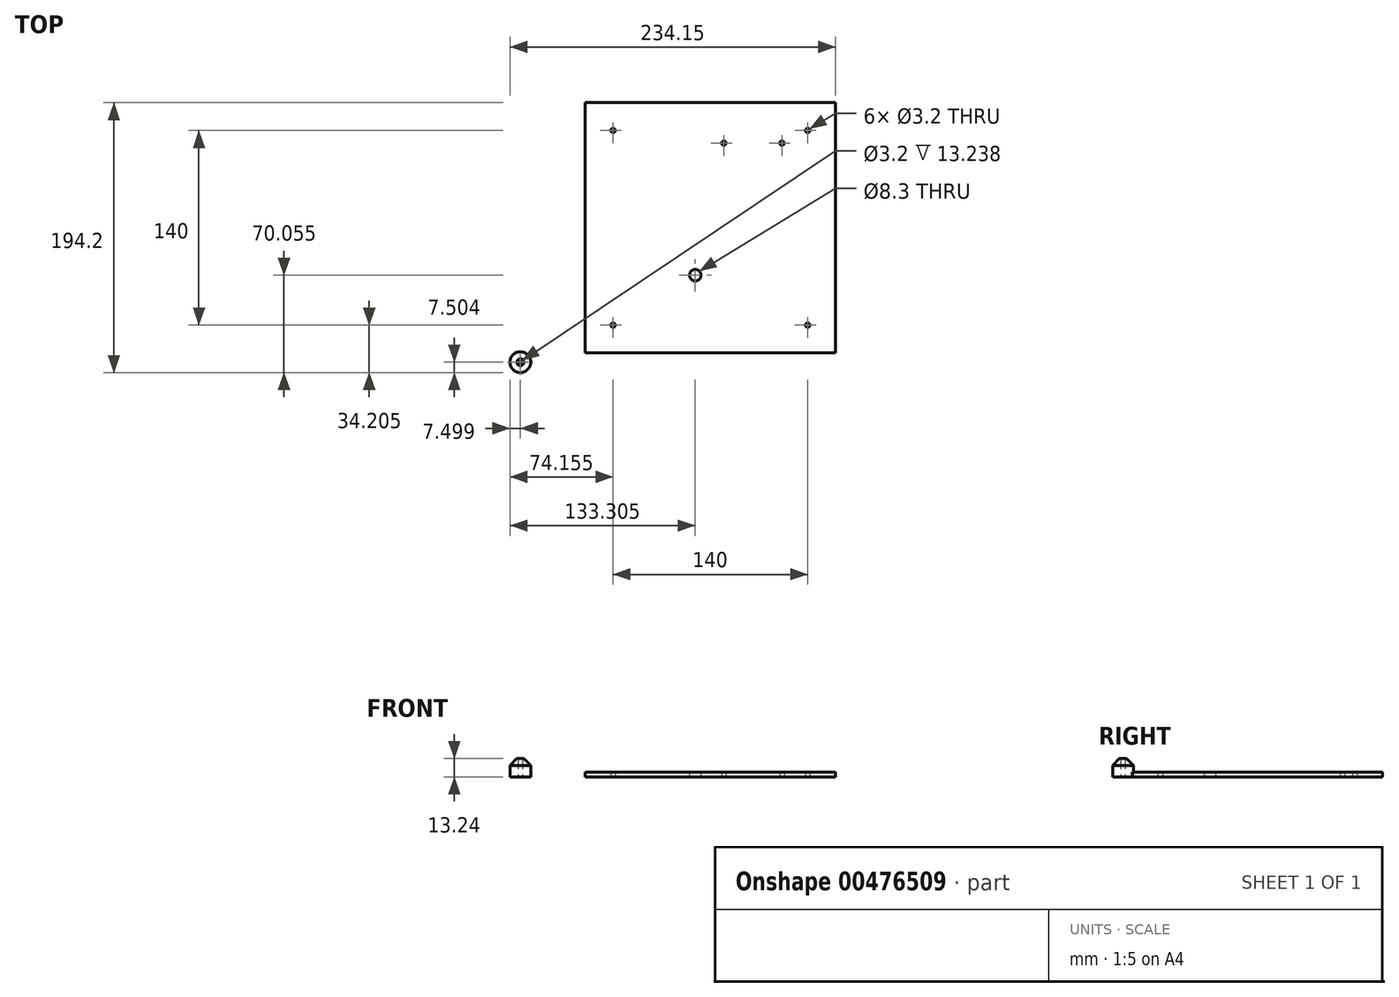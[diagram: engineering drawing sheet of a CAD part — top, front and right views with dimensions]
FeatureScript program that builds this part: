
annotation { "Feature Type Name" : "Feature", "Feature Type Description" : "" }
export const myFeature = defineFeature(function(context is Context, id is Id, definition is map)
    precondition{}
    {
        {
            var Q0;
            Q0=qCreatedBy(makeId("Top.planeOp"),FACE);
            var sketch = newSketch(context, id + "F0", { "sketchPlane" : qUnion([Q0])});
            skLineSegment(sketch, "E0", {"start": v(-49.64, -45.02) * mm, "end": v(130.36, -45.02) * mm});
            skLineSegment(sketch, "E1", {"start": v(130.36, -45.02) * mm, "end": v(130.36, 134.98) * mm});
            skLineSegment(sketch, "E2", {"start": v(130.36, 134.98) * mm, "end": v(-49.64, 134.98) * mm});
            skLineSegment(sketch, "E3", {"start": v(-49.64, 134.98) * mm, "end": v(-49.64, -45.02) * mm});
            skCircle(sketch, "E4", {"center": v(-29.64, 114.98) * mm, "radius": 1.6 * mm});
            skCircle(sketch, "E5", {"center": v(110.36, 114.98) * mm, "radius": 1.6 * mm});
            skCircle(sketch, "E6", {"center": v(-29.64, -25.02) * mm, "radius": 1.6 * mm});
            skCircle(sketch, "E7", {"center": v(110.36, -25.02) * mm, "radius": 1.6 * mm});
            skCircle(sketch, "E8", {"center": v(29.51, 10.83) * mm, "radius": 4.15 * mm});
            skSolve(sketch);
        }
        {
            var Q0;
            Q0=makeQuery(id+"F0.imprint","IMPRINT",FACE,{"disambiguationData":[TD([[makeQuery(id+"F0.imprint","IMPRINT",EDGE,{"derivedFrom":sQuery(id+"F0.wireOp",EDGE,"E0")}),1.0]])]});
            extrude(context, id + "F1", {"entities" : qUnion([Q0]), "depth" : 3.22 * mm, "offsetDistance" : 25 * mm});
        }
        {
            var Q0;
            Q0=qCreatedBy(makeId("Top.planeOp"),FACE);
            var sketch = newSketch(context, id + "F2", { "sketchPlane" : qUnion([Q0])});
            skCircle(sketch, "E9", {"center": v(50.04, 105.82) * mm, "radius": 1.6 * mm});
            skCircle(sketch, "E10", {"center": v(91.84, 105.82) * mm, "radius": 1.6 * mm});
            skSolve(sketch);
        }
        {
            var Q0;
            Q0 = qSketchRegion(id + "F2", true);
            extrude(context, id + "F3", {"entities" : qUnion([Q0]), "operationType" : NewBodyOperationType.REMOVE, "depth" : 25 * mm, "offsetDistance" : 25 * mm});
        }
        {
            var Q0;
            Q0=qCreatedBy(makeId("Top.planeOp"),FACE);
            var sketch = newSketch(context, id + "F4", { "sketchPlane" : qUnion([Q0])});
            skCircle(sketch, "E11", {"center": v(-96.3, -51.72) * mm, "radius": 7.5 * mm});
            skCircle(sketch, "E12", {"center": v(-96.3, -51.72) * mm, "radius": 1.6 * mm});
            skSolve(sketch);
        }
        {
            var Q0;
            Q0=makeQuery(id+"F4.imprint","IMPRINT",FACE,{"disambiguationData":[TD([[makeQuery(id+"F4.imprint","IMPRINT",EDGE,{"derivedFrom":sQuery(id+"F4.wireOp",EDGE,"E11")}),1.0]])]});
            extrude(context, id + "F5", {"entities" : qUnion([Q0]), "depth" : 13.24 * mm, "offsetDistance" : 25 * mm});
        }
        {
            var Q0;
            Q0=makeQuery(id+"F5.opExtrude","CAP_EDGE",EDGE,{"disambiguationData":[OSD([sQuery(id+"F4.wireOp",EDGE,"E11")])],"isStart":false});
            chamfer(context, id + "F6", {"entities" : qUnion([Q0]), "width" : 5 * mm, "tangentPropagation" : true});
        }
    });
